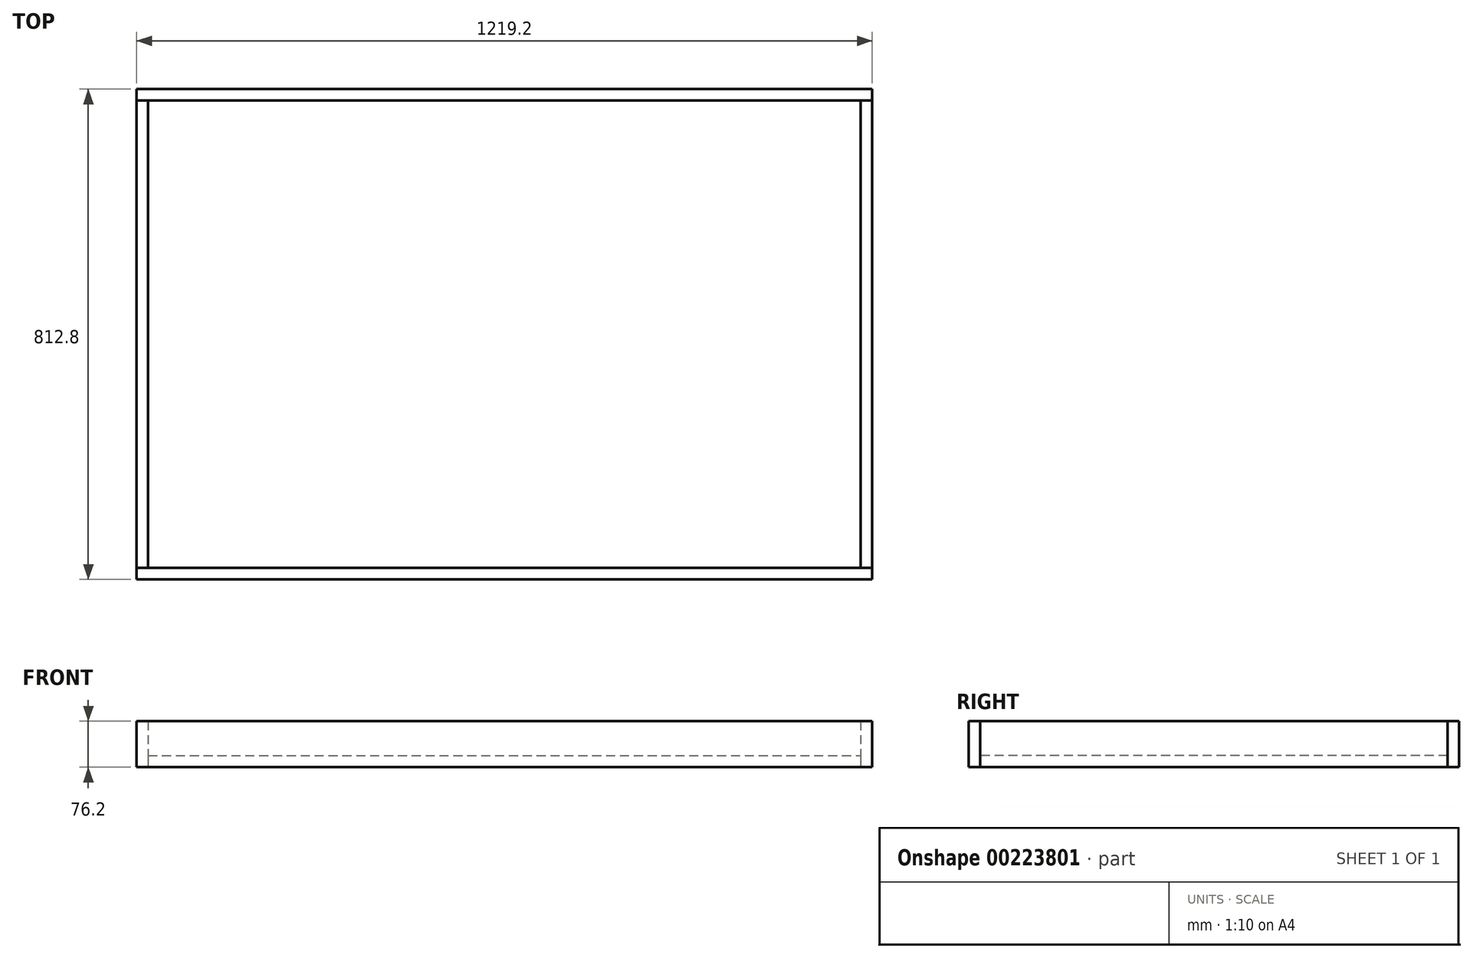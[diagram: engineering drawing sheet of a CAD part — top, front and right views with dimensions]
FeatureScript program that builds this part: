
annotation { "Feature Type Name" : "Feature", "Feature Type Description" : "" }
export const myFeature = defineFeature(function(context is Context, id is Id, definition is map)
    precondition{}
    {
        {
            var Q0;
            Q0=qCreatedBy(makeId("Front.planeOp"),FACE);
            var sketch = newSketch(context, id + "F0", { "sketchPlane" : qUnion([Q0])});
            skLineSegment(sketch, "E0", {"start": v(0, 76.2) * mm, "end": v(0, 0) * mm, "construction": true});
            skLineSegment(sketch, "E1", {"start": v(0, 0) * mm, "end": v(609.6, 0) * mm});
            skLineSegment(sketch, "E2", {"start": v(609.6, 0) * mm, "end": v(609.6, 76.2) * mm});
            skLineSegment(sketch, "E3", {"start": v(609.6, 76.2) * mm, "end": v(0, 76.2) * mm});
            skLineSegment(sketch, "E4", {"start": v(609.6, 19.05) * mm, "end": v(0, 19.05) * mm});
            skLineSegment(sketch, "E5", {"start": v(590.55, 76.2) * mm, "end": v(590.55, 19.05) * mm});
            skLineSegment(sketch, "E6.MirrorCS", {"start": v(-609.6, 0) * mm, "end": v(-609.6, 76.2) * mm});
            skLineSegment(sketch, "E7.MirrorCS", {"start": v(-609.6, 76.2) * mm, "end": v(0, 76.2) * mm});
            skLineSegment(sketch, "E8.MirrorCS", {"start": v(0, 0) * mm, "end": v(-609.6, 0) * mm});
            skLineSegment(sketch, "E9.MirrorCS", {"start": v(-590.55, 76.2) * mm, "end": v(-590.55, 19.05) * mm});
            skLineSegment(sketch, "E10.MirrorCS", {"start": v(-609.6, 19.05) * mm, "end": v(0, 19.05) * mm});
            skLineSegment(sketch, "E11", {"start": v(609.6, 76.2) * mm, "end": v(609.6, 101.6) * mm, "construction": true});
            skLineSegment(sketch, "E12", {"start": v(609.6, 101.6) * mm, "end": v(-609.6, 101.6) * mm, "construction": true});
            skLineSegment(sketch, "E13", {"start": v(-609.6, 101.6) * mm, "end": v(-609.6, 76.2) * mm, "construction": true});
            skSolve(sketch);
        }
        {
            var Q0;
            Q0=qCreatedBy(makeId("Top.planeOp"),FACE);
            var sketch = newSketch(context, id + "F1", { "sketchPlane" : qUnion([Q0])});
            skLineSegment(sketch, "E14.bottom", {"start": v(-609.6, 406.4) * mm, "end": v(609.6, 406.4) * mm});
            skLineSegment(sketch, "E14.top", {"start": v(-609.6, -406.4) * mm, "end": v(609.6, -406.4) * mm});
            skLineSegment(sketch, "E14.left", {"start": v(-609.6, 406.4) * mm, "end": v(-609.6, -406.4) * mm});
            skLineSegment(sketch, "E14.right", {"start": v(609.6, 406.4) * mm, "end": v(609.6, -406.4) * mm});
            skLineSegment(sketch, "E15", {"start": v(0, 0) * mm, "end": v(609.6, 0) * mm, "construction": true});
            skLineSegment(sketch, "E16.0", {"start": v(-590.55, 387.35) * mm, "end": v(590.55, 387.35) * mm});
            skLineSegment(sketch, "E16.1", {"start": v(-590.55, 387.35) * mm, "end": v(-590.55, -387.35) * mm});
            skLineSegment(sketch, "E16.2", {"start": v(-590.55, -387.35) * mm, "end": v(590.55, -387.35) * mm});
            skLineSegment(sketch, "E16.3", {"start": v(590.55, 387.35) * mm, "end": v(590.55, -387.35) * mm});
            skLineSegment(sketch, "E17", {"start": v(-590.55, -387.35) * mm, "end": v(-609.6, -387.35) * mm});
            skLineSegment(sketch, "E18", {"start": v(590.55, -387.35) * mm, "end": v(609.6, -387.35) * mm});
            skLineSegment(sketch, "E19", {"start": v(590.55, 387.35) * mm, "end": v(609.6, 387.35) * mm});
            skLineSegment(sketch, "E20", {"start": v(-590.55, 387.35) * mm, "end": v(-609.6, 387.35) * mm});
            skSolve(sketch);
        }
        {
            var Q0;
            Q0=qCreatedBy(makeId("Top.planeOp"),FACE);
            var sketch = newSketch(context, id + "F2", { "sketchPlane" : qUnion([Q0])});
            skLineSegment(sketch, "E21.0", {"start": v(-590.55, 387.35) * mm, "end": v(-590.55, -387.35) * mm});
            skLineSegment(sketch, "E21.1", {"start": v(-590.55, 387.35) * mm, "end": v(590.55, 387.35) * mm});
            skLineSegment(sketch, "E21.2", {"start": v(590.55, 387.35) * mm, "end": v(590.55, -387.35) * mm});
            skLineSegment(sketch, "E21.3", {"start": v(-590.55, -387.35) * mm, "end": v(590.55, -387.35) * mm});
            skSolve(sketch);
        }
        {
            var Q0;
            Q0 = qSketchRegion(id + "F2", true);
            var Q1;
            Q1=sQuery(id+"F0.wireOp",VERTEX,"E4.start");
            extrude(context, id + "F3", {"entities" : qUnion([Q0]), "endBound" : BoundingType.UP_TO_VERTEX, "endBoundEntityVertex" : qUnion([Q1]), "depth" : 25.4 * mm});
        }
        {
            var Q0;
            Q0=qCreatedBy(makeId("Top.planeOp"),FACE);
            var sketch = newSketch(context, id + "F4", { "sketchPlane" : qUnion([Q0])});
            skLineSegment(sketch, "E22.0", {"start": v(-590.55, -387.35) * mm, "end": v(590.55, -387.35) * mm});
            skLineSegment(sketch, "E22.1.0", {"start": v(590.55, -387.35) * mm, "end": v(-590.55, -387.35) * mm});
            skLineSegment(sketch, "E22.1.1", {"start": v(-590.55, -387.35) * mm, "end": v(-609.6, -387.35) * mm});
            skLineSegment(sketch, "E22.1.2", {"start": v(-609.6, -387.35) * mm, "end": v(-609.6, -406.4) * mm});
            skLineSegment(sketch, "E22.1.3", {"start": v(-609.6, -406.4) * mm, "end": v(609.6, -406.4) * mm});
            skLineSegment(sketch, "E22.1.4", {"start": v(609.6, -406.4) * mm, "end": v(609.6, -387.35) * mm});
            skLineSegment(sketch, "E22.1.5", {"start": v(609.6, -387.35) * mm, "end": v(590.55, -387.35) * mm});
            skLineSegment(sketch, "E23.0.0", {"start": v(-609.6, 387.35) * mm, "end": v(-590.55, 387.35) * mm});
            skLineSegment(sketch, "E23.0.1", {"start": v(-590.55, 387.35) * mm, "end": v(590.55, 387.35) * mm});
            skLineSegment(sketch, "E23.0.2", {"start": v(590.55, 387.35) * mm, "end": v(609.6, 387.35) * mm});
            skLineSegment(sketch, "E23.0.3", {"start": v(609.6, 387.35) * mm, "end": v(609.6, 406.4) * mm});
            skLineSegment(sketch, "E23.0.4", {"start": v(609.6, 406.4) * mm, "end": v(-609.6, 406.4) * mm});
            skLineSegment(sketch, "E23.0.5", {"start": v(-609.6, 406.4) * mm, "end": v(-609.6, 387.35) * mm});
            skSolve(sketch);
        }
        {
            var Q0;
            Q0 = qSketchRegion(id + "F4", true);
            var Q1;
            Q1=sQuery(id+"F0.wireOp",VERTEX,"E3.start");
            extrude(context, id + "F5", {"entities" : qUnion([Q0]), "endBound" : BoundingType.UP_TO_VERTEX, "endBoundEntityVertex" : qUnion([Q1]), "depth" : 25.4 * mm});
        }
        {
            var Q0;
            Q0=makeQuery(id+"F5.opExtrude","CAP_FACE",FACE,{"disambiguationData":[OSD([dummyQuery(id+"F5.vertexPlane.planeOp",FACE)]),ownerDisambiguation([makeQuery(id+"F5.opExtrude","SWEPT_BODY",BODY,{"disambiguationData":[OSD([sQuery(id+"F4.wireOp",EDGE,"E22.1.0"),sQuery(id+"F4.wireOp",EDGE,"E22.1.1"),sQuery(id+"F4.wireOp",EDGE,"E22.1.2"),sQuery(id+"F4.wireOp",EDGE,"E22.1.3"),sQuery(id+"F4.wireOp",EDGE,"E22.1.4"),sQuery(id+"F4.wireOp",EDGE,"E22.1.5")])]})])],"isStart":false});
            var sketch = newSketch(context, id + "F6", { "sketchPlane" : qUnion([Q0])});
            skLineSegment(sketch, "E24.0", {"start": v(-609.6, -406.4) * mm, "end": v(609.6, -406.4) * mm});
            skLineSegment(sketch, "E24.1", {"start": v(609.6, -387.35) * mm, "end": v(-609.6, -387.35) * mm});
            skLineSegment(sketch, "E24.2", {"start": v(-609.6, -387.35) * mm, "end": v(-609.6, -406.4) * mm});
            skLineSegment(sketch, "E24.3", {"start": v(609.6, -406.4) * mm, "end": v(609.6, -387.35) * mm});
            skSolve(sketch);
        }
        {
            var Q0;
            Q0=qCreatedBy(makeId("Top.planeOp"),FACE);
            var sketch = newSketch(context, id + "F7", { "sketchPlane" : qUnion([Q0])});
            skLineSegment(sketch, "E25.0.0", {"start": v(609.6, -387.35) * mm, "end": v(609.6, 387.35) * mm});
            skLineSegment(sketch, "E25.0.1", {"start": v(609.6, 387.35) * mm, "end": v(590.55, 387.35) * mm});
            skLineSegment(sketch, "E25.0.2", {"start": v(590.55, 387.35) * mm, "end": v(590.55, -387.35) * mm});
            skLineSegment(sketch, "E25.0.3", {"start": v(590.55, -387.35) * mm, "end": v(609.6, -387.35) * mm});
            skLineSegment(sketch, "E26.0.0", {"start": v(-609.6, -387.35) * mm, "end": v(-590.55, -387.35) * mm});
            skLineSegment(sketch, "E26.0.1", {"start": v(-590.55, -387.35) * mm, "end": v(-590.55, 387.35) * mm});
            skLineSegment(sketch, "E26.0.2", {"start": v(-590.55, 387.35) * mm, "end": v(-609.6, 387.35) * mm});
            skLineSegment(sketch, "E26.0.3", {"start": v(-609.6, 387.35) * mm, "end": v(-609.6, -387.35) * mm});
            skSolve(sketch);
        }
        {
            var Q0;
            Q0 = qSketchRegion(id + "F7", true);
            var Q1;
            Q1=sQuery(id+"F0.wireOp",VERTEX,"E3.start");
            extrude(context, id + "F8", {"entities" : qUnion([Q0]), "endBound" : BoundingType.UP_TO_VERTEX, "endBoundEntityVertex" : qUnion([Q1]), "depth" : 25.4 * mm});
        }
    });
